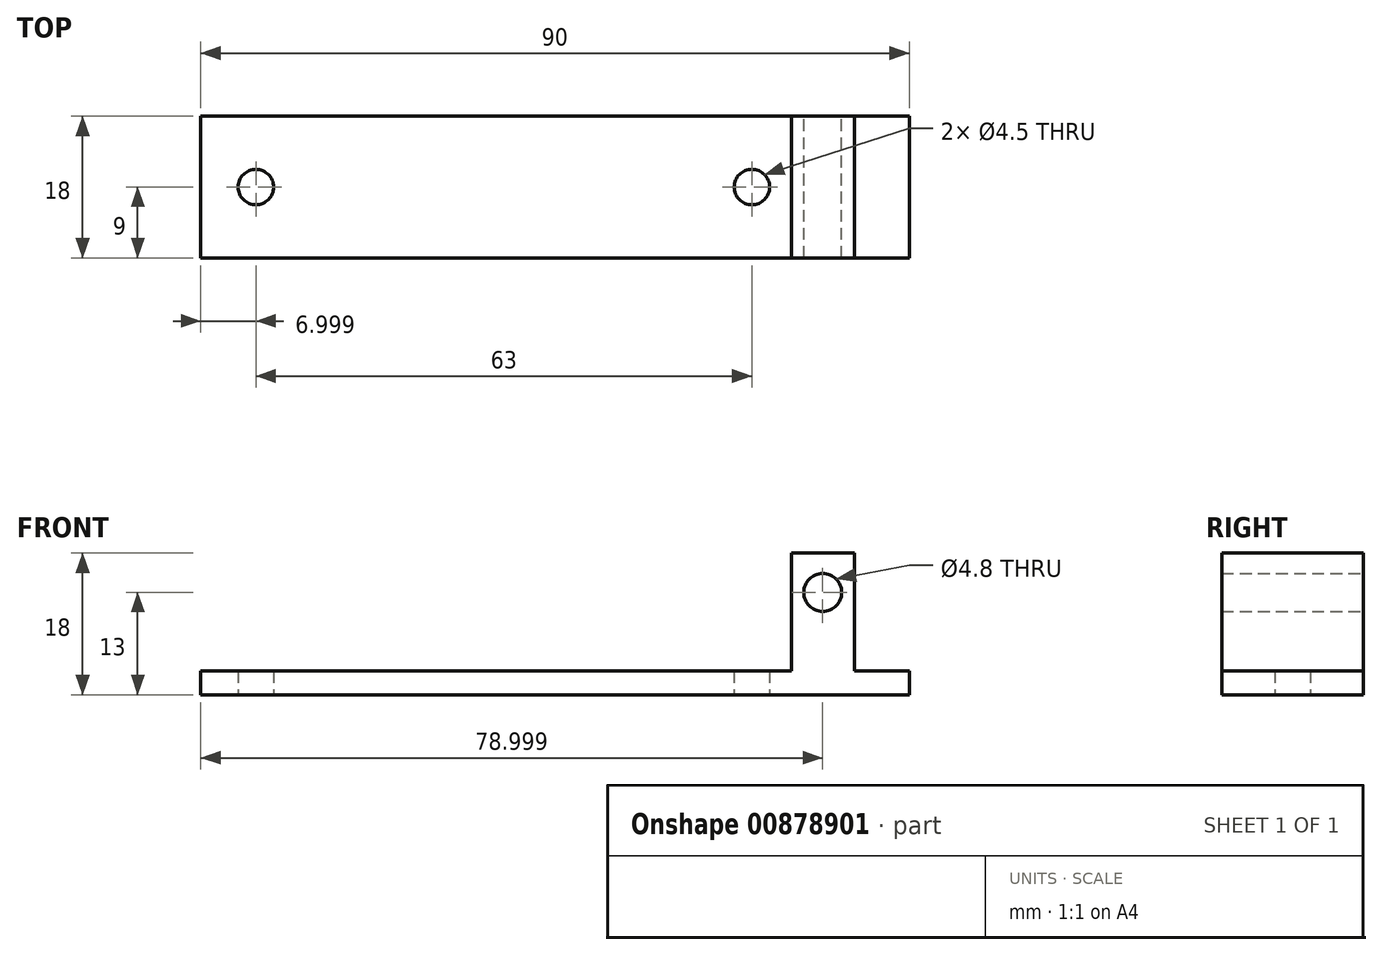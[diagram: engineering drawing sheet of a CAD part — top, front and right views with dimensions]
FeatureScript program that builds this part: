
annotation { "Feature Type Name" : "Feature", "Feature Type Description" : "" }
export const myFeature = defineFeature(function(context is Context, id is Id, definition is map)
    precondition{}
    {
        {
            var Q0;
            Q0=qCreatedBy(makeId("Top.planeOp"),FACE);
            var sketch = newSketch(context, id + "F0", { "sketchPlane" : qUnion([Q0])});
            skCircle(sketch, "E0", {"center": v(-34.68, 0) * mm, "radius": 2.25 * mm});
            skCircle(sketch, "E1", {"center": v(28.32, 0) * mm, "radius": 2.25 * mm});
            skPoint(sketch, "E2.middle", {"position": v(0, 0) * mm});
            skLineSegment(sketch, "E3.bottom", {"start": v(-41.68, 9) * mm, "end": v(48.32, 9) * mm});
            skLineSegment(sketch, "E3.top", {"start": v(-41.68, -9) * mm, "end": v(48.32, -9) * mm});
            skLineSegment(sketch, "E3.left", {"start": v(-41.68, 9) * mm, "end": v(-41.68, -9) * mm});
            skLineSegment(sketch, "E3.right", {"start": v(48.32, 9) * mm, "end": v(48.32, -9) * mm});
            skSolve(sketch);
        }
        {
            var Q0;
            Q0=makeQuery(id+"F0.imprint","IMPRINT",FACE,{"disambiguationData":[TD([[makeQuery(id+"F0.imprint","IMPRINT",EDGE,{"derivedFrom":sQuery(id+"F0.wireOp",EDGE,"E0")}),-1.0]])]});
            extrude(context, id + "F1", {"entities" : qUnion([Q0]), "depth" : 3 * mm, "offsetDistance" : 25 * mm});
        }
        {
            var Q0;
            Q0=makeQuery(id+"F1.opExtrude","CAP_FACE",FACE,{"disambiguationData":[OSD([sQuery(id+"F0.wireOp",EDGE,"E0"),sQuery(id+"F0.wireOp",EDGE,"E1"),sQuery(id+"F0.wireOp",EDGE,"E3.bottom"),sQuery(id+"F0.wireOp",EDGE,"E3.top"),sQuery(id+"F0.wireOp",EDGE,"E3.left"),sQuery(id+"F0.wireOp",EDGE,"E3.right")])],"isStart":false});
            var sketch = newSketch(context, id + "F2", { "sketchPlane" : qUnion([Q0])});
            skLineSegment(sketch, "E4.bottom", {"start": v(33.32, 9) * mm, "end": v(41.32, 9) * mm});
            skLineSegment(sketch, "E4.top", {"start": v(33.32, -9) * mm, "end": v(41.32, -9) * mm});
            skLineSegment(sketch, "E4.left", {"start": v(33.32, 9) * mm, "end": v(33.32, -9) * mm});
            skLineSegment(sketch, "E4.right", {"start": v(41.32, 9) * mm, "end": v(41.32, -9) * mm});
            skCircle(sketch, "E5", {"center": v(-34.68, 0) * mm, "radius": 2.25 * mm});
            skLineSegment(sketch, "E6", {"start": v(-41.68, 9) * mm, "end": v(-41.68, -9) * mm});
            skLineSegment(sketch, "E7", {"start": v(-41.68, 9) * mm, "end": v(48.32, 9) * mm});
            skLineSegment(sketch, "E8", {"start": v(48.32, 9) * mm, "end": v(48.32, -9) * mm});
            skLineSegment(sketch, "E9", {"start": v(-41.68, -9) * mm, "end": v(48.32, -9) * mm});
            skCircle(sketch, "E10", {"center": v(28.32, 0) * mm, "radius": 2.25 * mm});
            skSolve(sketch);
        }
        {
            var Q0;
            {var subQ0=sQuery(id+"F2.wireOp",EDGE,"E4.left");Q0=makeQuery(id+"F2.imprint","IMPRINT",FACE,{"disambiguationData":[TD([[makeQuery(id+"F2.imprint","IMPRINT",EDGE,{"derivedFrom":subQ0}),1.0]])]});}
            extrude(context, id + "F3", {"entities" : qUnion([Q0]), "operationType" : NewBodyOperationType.ADD, "depth" : 15 * mm, "offsetDistance" : 25 * mm});
        }
        {
            var Q0;
            Q0=makeQuery(id+"F3.boolean.opBoolean","MERGE",FACE,{"derivedFrom":[makeQuery(id+"F1.opExtrude","SWEPT_FACE",FACE,{"disambiguationData":[OSD([sQuery(id+"F0.wireOp",EDGE,"E3.bottom")])]}),makeQuery(id+"F3.opExtrude","SWEPT_FACE",FACE,{"disambiguationData":[OSD([sQuery(id+"F2.wireOp",EDGE,"E7")])]})]});
            var sketch = newSketch(context, id + "F4", { "sketchPlane" : qUnion([Q0])});
            skCircle(sketch, "E11", {"center": v(-37.32, 13) * mm, "radius": 2.4 * mm});
            skSolve(sketch);
        }
        {
            var Q0;
            Q0=makeQuery(id+"F4.imprint","IMPRINT",FACE,{"disambiguationData":[TD([[makeQuery(id+"F4.imprint","IMPRINT",EDGE,{"derivedFrom":sQuery(id+"F4.wireOp",EDGE,"E11")}),1.0]])]});
            extrude(context, id + "F5", {"entities" : qUnion([Q0]), "operationType" : NewBodyOperationType.REMOVE, "endBound" : BoundingType.UP_TO_NEXT, "oppositeDirection" : true, "depth" : 25 * mm, "offsetDistance" : 25 * mm});
        }
    });
